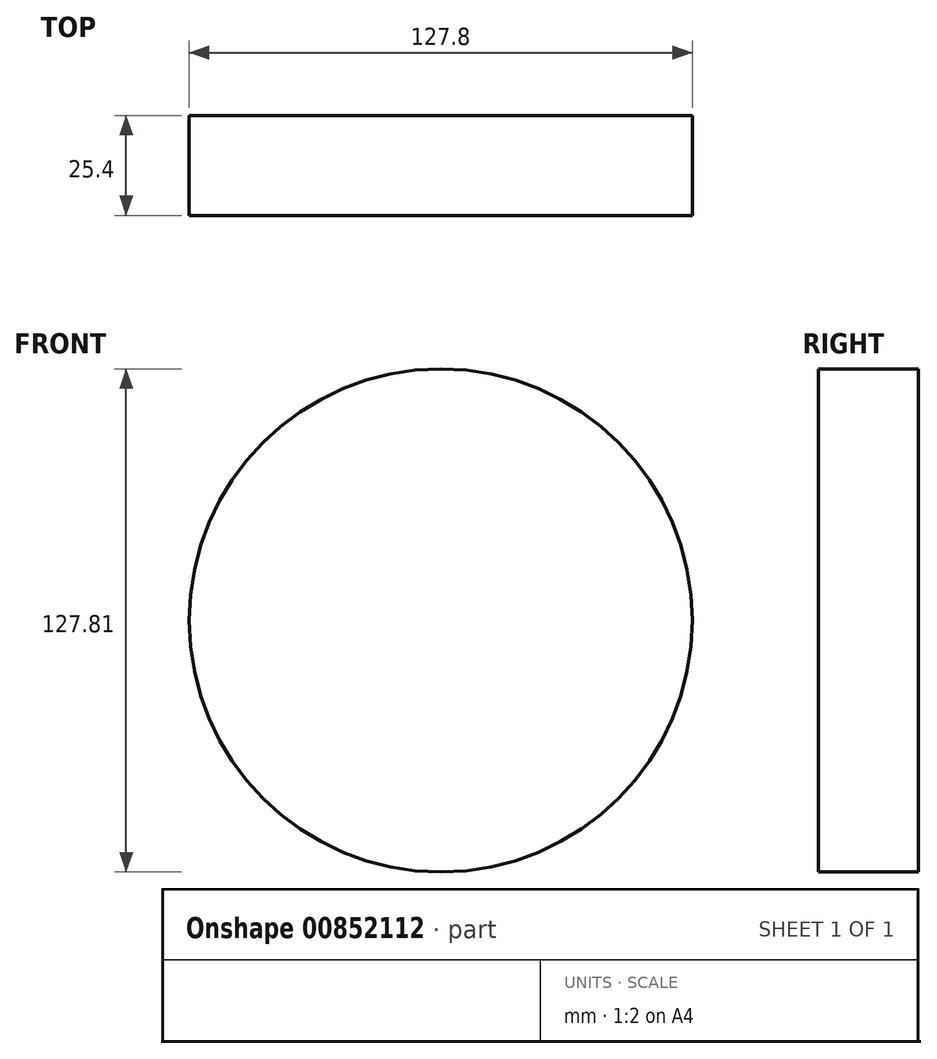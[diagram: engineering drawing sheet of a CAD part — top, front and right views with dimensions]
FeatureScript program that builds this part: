
annotation { "Feature Type Name" : "Feature", "Feature Type Description" : "" }
export const myFeature = defineFeature(function(context is Context, id is Id, definition is map)
    precondition{}
    {
        {
            var Q0;
            Q0=qCreatedBy(makeId("Front.planeOp"),FACE);
            var sketch = newSketch(context, id + "F0", { "sketchPlane" : qUnion([Q0])});
            skCircle(sketch, "E0", {"center": v(8.33, 8.63) * mm, "radius": 63.9 * mm});
            skSolve(sketch);
        }
        {
            var Q0;
            Q0 = qSketchRegion(id + "F0", true);
            extrude(context, id + "F1", {"entities" : qUnion([Q0]), "depth" : 25.4 * mm, "offsetDistance" : 25.4 * mm});
        }
    });
